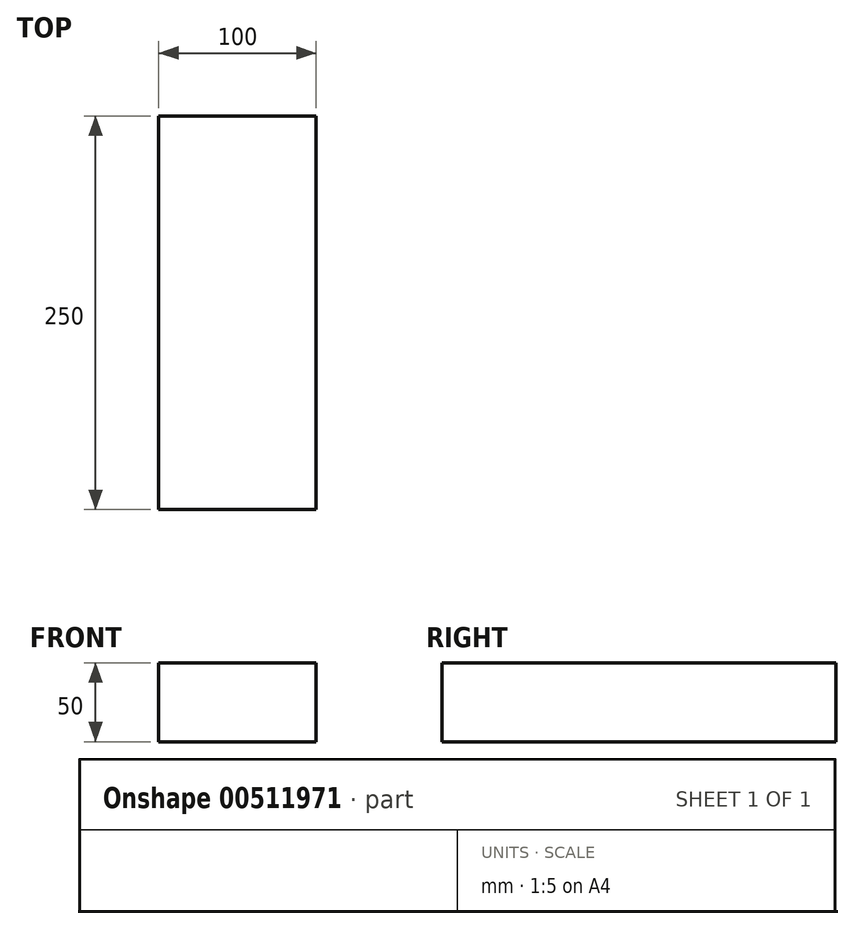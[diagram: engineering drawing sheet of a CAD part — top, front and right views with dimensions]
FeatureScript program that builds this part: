
annotation { "Feature Type Name" : "Feature", "Feature Type Description" : "" }
export const myFeature = defineFeature(function(context is Context, id is Id, definition is map)
    precondition{}
    {
        {
            var Q0;
            Q0=qCreatedBy(makeId("Top.planeOp"),FACE);
            var sketch = newSketch(context, id + "F0", { "sketchPlane" : qUnion([Q0])});
            skLineSegment(sketch, "E0.bottom", {"start": v(0, 0) * mm, "end": v(100, 0) * mm});
            skLineSegment(sketch, "E0.top", {"start": v(0, 250) * mm, "end": v(100, 250) * mm});
            skLineSegment(sketch, "E0.left", {"start": v(0, 0) * mm, "end": v(0, 250) * mm});
            skLineSegment(sketch, "E0.right", {"start": v(100, 0) * mm, "end": v(100, 250) * mm});
            skSolve(sketch);
        }
        {
            var Q0;
            Q0=makeQuery(id+"F0.imprint","IMPRINT",FACE,{"disambiguationData":[TD([[makeQuery(id+"F0.imprint","IMPRINT",EDGE,{"derivedFrom":sQuery(id+"F0.wireOp",EDGE,"E0.bottom")}),1.0]])]});
            extrude(context, id + "F1", {"entities" : qUnion([Q0]), "depth" : 50 * mm});
        }
    });
